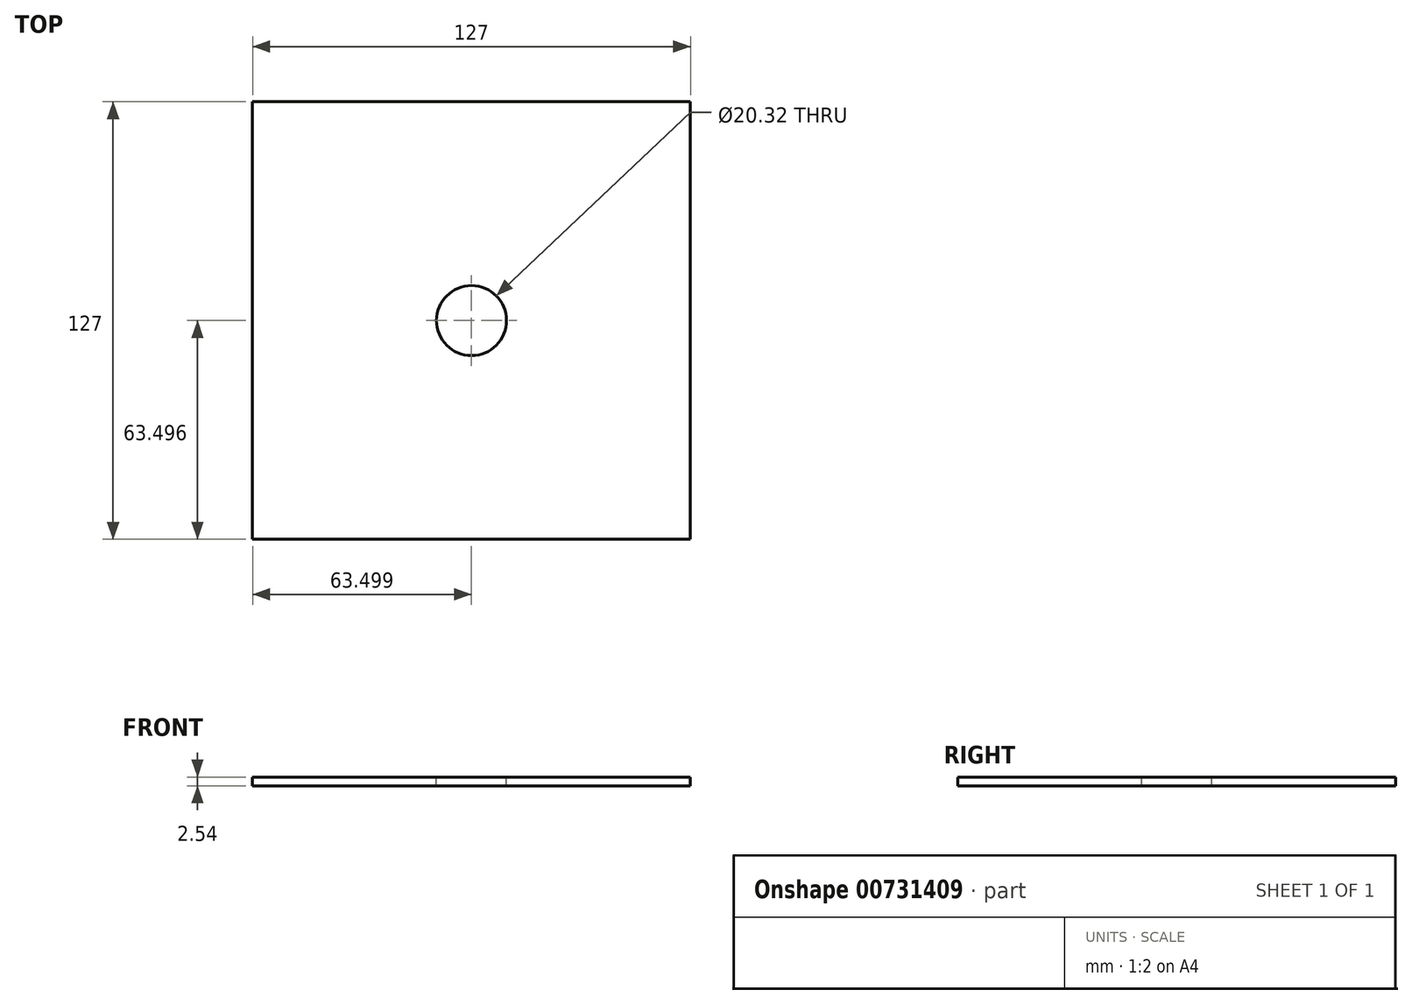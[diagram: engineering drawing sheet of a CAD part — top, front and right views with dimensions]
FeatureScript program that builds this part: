
annotation { "Feature Type Name" : "Feature", "Feature Type Description" : "" }
export const myFeature = defineFeature(function(context is Context, id is Id, definition is map)
    precondition{}
    {
        {
            var Q0;
            Q0=qCreatedBy(makeId("Top.planeOp"),FACE);
            var sketch = newSketch(context, id + "F0", { "sketchPlane" : qUnion([Q0])});
            skLineSegment(sketch, "E0.bottom", {"start": v(-41.83, -40.5) * mm, "end": v(85.17, -40.5) * mm});
            skLineSegment(sketch, "E0.top", {"start": v(-41.83, 86.5) * mm, "end": v(85.17, 86.5) * mm});
            skLineSegment(sketch, "E0.left", {"start": v(-41.83, -40.5) * mm, "end": v(-41.83, 86.5) * mm});
            skLineSegment(sketch, "E0.right", {"start": v(85.17, -40.5) * mm, "end": v(85.17, 86.5) * mm});
            skSolve(sketch);
        }
        {
            var Q0;
            Q0=makeQuery(id+"F0.imprint","IMPRINT",FACE,{"disambiguationData":[TD([[makeQuery(id+"F0.imprint","IMPRINT",EDGE,{"derivedFrom":sQuery(id+"F0.wireOp",EDGE,"E0.bottom")}),1.0]])]});
            var Q1;
            Q1 = qSketchRegion(id + "F0", true);
            extrude(context, id + "F1", {"entities" : qUnion([Q0, Q1]), "depth" : 2.54 * mm, "offsetDistance" : 25.4 * mm});
        }
        {
            var Q0;
            Q0=makeQuery(id+"F1.opExtrude","CAP_FACE",FACE,{"disambiguationData":[OSD([sQuery(id+"F0.wireOp",EDGE,"E0.bottom"),sQuery(id+"F0.wireOp",EDGE,"E0.top"),sQuery(id+"F0.wireOp",EDGE,"E0.left"),sQuery(id+"F0.wireOp",EDGE,"E0.right")])],"isStart":false});
            var sketch = newSketch(context, id + "F2", { "sketchPlane" : qUnion([Q0])});
            skLineSegment(sketch, "E1", {"start": v(21.67, -40.5) * mm, "end": v(21.67, 23) * mm});
            skLineSegment(sketch, "E2", {"start": v(85.17, 23) * mm, "end": v(21.67, 23) * mm});
            skCircle(sketch, "E3", {"center": v(21.67, 23) * mm, "radius": 10.16 * mm});
            skSolve(sketch);
        }
        {
            var Q0;
            Q0=sQuery(id+"F2.wireOp",VERTEX,"E3.center");
            var Q1;
            Q1=makeQuery(id+"F1.opExtrude","SWEPT_BODY",BODY,{"disambiguationData":[OSD([sQuery(id+"F0.wireOp",EDGE,"E0.bottom"),sQuery(id+"F0.wireOp",EDGE,"E0.top"),sQuery(id+"F0.wireOp",EDGE,"E0.left"),sQuery(id+"F0.wireOp",EDGE,"E0.right")])]});
            hole(context, id + "F3", {"style" : HoleStyle.SIMPLE, "endStyle" : HoleEndStyle.THROUGH, "holeDiameter" : 20.32 * mm, "majorDiameter" : 6.35 * mm, "isTappedThrough" : true, "tappedDepth" : 12.7 * mm, "tapClearance" : 3, "locations" : qUnion([Q0]), "scope" : qUnion([Q1])});
        }
    });
